# Revit family: Sarlam_Eclairage_Borne_Chartres_Infini_T2_Diam_420mm_4000Lm
name_source: partatom
category: Luminaires
units: mm (PartAtom-declared; Revit-internal decimal feet)

## family parameters
Basée sur le plan de construction = Non
Cote de connecteur circulaire = Utiliser le diamètre
Couper avec des vides une fois chargée = Non
Partagée = Non
Point de calcul de pièce = Non
Source d'éclairage = Non
Toujours verticalement = Oui
Type d'élément = Normal

## types (4) — shared parameters
Angle du faisceau = Faisceau libre
Appareillage = Appareil à LED commandé en courant
Classe de protection = II
Condition Générale d'Utilisation = https://export.legrand.com
Couleur du boîtier/corps = LEGRAND - Blanc
Diamètre externe = 420 mm  [stored 1.37795 ft]
Douille = Sans
Fabricant = LEGRAND
Flux lumineux utile lm = 4000
Hauteur/profondeur = 90 mm  [stored 0.295276 ft]
Indice de protection (IP) = IP55
Indice de protection contre les chocs (IK) = IK10
Indice de rendu des couleurs CRI = 80-89
Largeur = 420 mm  [stored 1.37795 ft]
Longueur = 420 mm  [stored 1.37795 ft]
Matériau du boîtier/corps = Plastique
Puissance de la lampe en Multiwatt = 35/49W
Répartition lumineuse = Symétrique
Source lumineuse = Led non interchangeable
Température de couleur K MAX = 4000
Température de couleur K MIN = 4000
Tension nominale (Un) V MAX = 253
Tension nominale (Un) V MIN = 207
Type de tension = CA
URL = http://www.legrandoc.com
URL Hublot = http://www.legrandoc.com
zero-valued in all types: Courant nominal mA MAX, Courant nominal mA MIN, Elévation par défaut, Puissance du système W

## per-type parameters (varying)
| type | Avec détecteur crépusculaire | Avec détecteur de mouvement | Description | Hauteur borne | Hauteur pieds | Hublot | Modèle | Type de variation |
| Borne 600 + ON/OFF BLANC | Non | Non | BORNE CHARTRES INFINI HAUTEUR 600 + CHARTRES INFINI 4500LM 4000K STANDARD ON/OFF BLANC | 600 mm | 524 mm | Legrand-Eclairage-Hublot-Chartres Infini-T2 Diam 420mm-4000Lm : ON/OFF BLANC | SL-532030 + SL-532088 | Non régulable |
| Borne 1200 + ON/OFF BLANC | Non | Non | BORNE CHARTRES INFINI HAUTEUR 1200 + CHARTRES INFINI 4500LM 4000K STANDARD ON/OFF BLANC | 1200 mm | 1124 mm  [stored 3.68766 ft] | Legrand-Eclairage-Hublot-Chartres Infini-T2 Diam 420mm-4000Lm : ON/OFF BLANC | SL-532033 + SL-532088 | Non régulable |
| Borne 600 + Détection BLANC | Oui | Oui | BORNE CHARTRES INFINI HAUTEUR 600 + CHARTRES INFINI 4500LM 4000K STANDARD DETECTION HF BLANC | 600 mm | 524 mm | Legrand-Eclairage-Hublot-Chartres Infini-T2 Diam 420mm-4000Lm : Détection BLANC | SL-532030 + SL-532089 | Autre |
| Borne 1200 + Détection BLANC | Oui | Oui | BORNE CHARTRES INFINI HAUTEUR 1200 + CHARTRES INFINI 4500LM 4000K STANDARD DETECTION HF BLANC | 1200 mm | 1124 mm  [stored 3.68766 ft] | Legrand-Eclairage-Hublot-Chartres Infini-T2 Diam 420mm-4000Lm : Détection BLANC | SL-532033 + SL-532089 | Autre |

note: [stored X ft] marks values corroborated as IEEE doubles in the binary element streams (Revit-internal decimal feet)

## geometry (parser evidence)
native form markers: Blend x14
no freeform markers — native parametric forms only
